# Revit family: Door_AcousticSteel_Ambico_Double-Vision
name_source: partatom
category: Doors
units: mm (PartAtom-declared; Revit-internal decimal feet)

## family parameters
Always vertical = Yes
Classification Number = 23.30.10.21.17.14
Cut with Voids When Loaded = No
Host = Wall
Room Calculation Point = No
Shared = No

## types (1)
- ByType
    ADA Compliant = Yes
    AppliedPanel = Yes
    Construction Details = http://www.arcat.com
    Description = Ambico Door as Specified
    Expected Lifespan (Years) = 0
    Fire Rating = As Specified in 08300
    Frame Finish = Metal - Steel - Ambico - Painted - Blue
    Frame Thickness = 0' - 5 7/8"
    Frame Width = 0' - 2"
    Function = Interior
    Glass Thickness = 0' - 1 1/2"
    Glass Type = Glass - Glazing - Ambico - Clear
    Green Building-LEED = http://www.arcat.com
    Hardware Finish = Metal - Stainless Steel - Ambico - 4 Finish
    Height = 7' - 0"
    HighSTCFrame = Yes
    Installation-Fabrication = http://www.ambico.com
    Keynote = 08300
    Large Trim = No
    Maintenance Schedule (Months) = 0
    Manufacturer = Ambico Limited
    Manufacturer Fax = 800-465-8561
    Manufacturer Website = http://www.ambico.com
    Model = As Specified
    Panel Height = 6' - 11 3/4"
    Panel Material = Metal - Steel - Ambico - Painted - Blue
    Panel Width = 3' - 0"
    Product Data = http://www.arcat.com
    RO Offset = 0' - 0"
    R_Value = 0
    Rough Height = 7' - 0"
    Rough Width = 6' - 0"
    STCValue = 54
    Sales Information = http://www.ambico.com
    Send Message = http://www.arcat.com Limited&coid=40356&rep=119&fax=800-465-8561&mf=
    Small Trim = No
    SmallAstrigal = No
    Sound Transmission Class (STC) = 55
    Specification = http://www.arcat.com
    StandardFrame = No
    Thickness = 0' - 1 3/4"
    URL = http://www.ambico.com
    Wall Closure = By host
    Warranty Duration (Years) = 0
    Width = 6' - 0"
    ofst = 0' - 1"

## geometry (parser evidence)
native form markers: Blend x12, Sweep x14
no freeform markers — native parametric forms only
